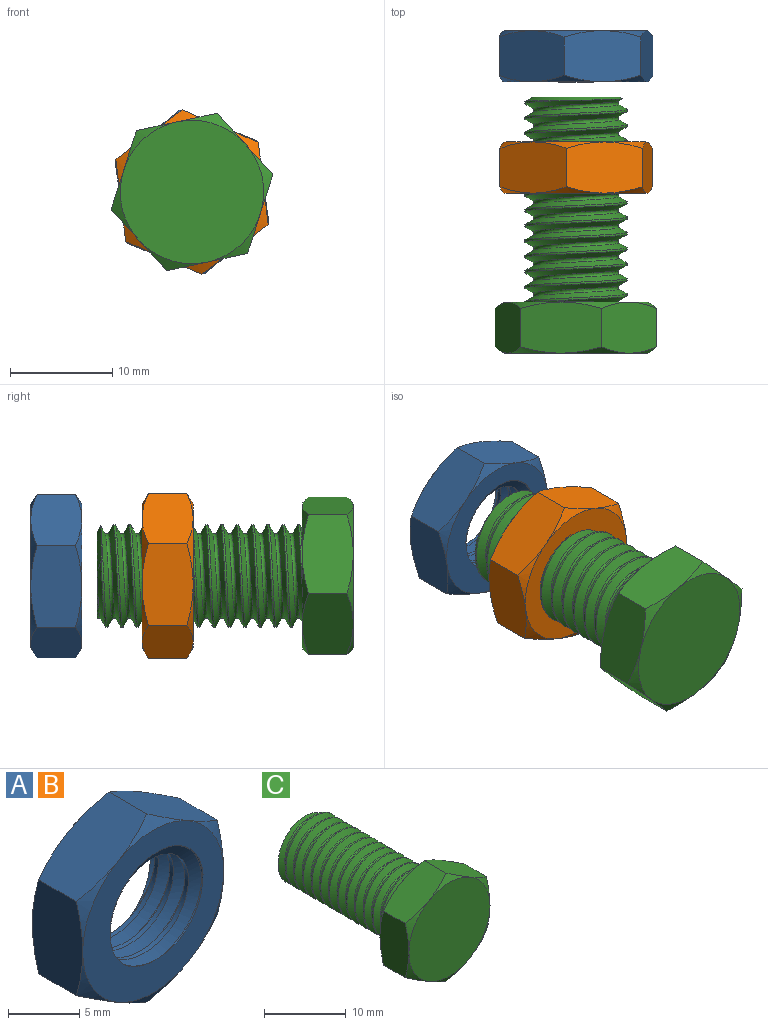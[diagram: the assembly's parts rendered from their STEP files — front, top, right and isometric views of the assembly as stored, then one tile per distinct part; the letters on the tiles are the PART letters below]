
ASSEMBLY  parts=3 mates=2
PART A: 24 faces, bbox 16.8x7x16.8 mm
  f0: plane 14.44x14.44mm, normal (0,-1,0), area 86.9mm2, adj f8,f9,f10,f11,f18,f19,f20,f21
  f1: plane 14.44x14.44mm, normal (0,1,0), area 86.9mm2, adj f8,f9,f10,f11,f12,f13,f14,f15
  f2: plane 7.66x5.67mm, normal (0.5,0,-0.87), area 36.9mm2, adj f3,f7,f13,f17,f19,f23
  f3: plane 8.76x5.67mm, normal (1,0,0), area 36.9mm2, adj f2,f4,f16,f17,f22,f23
  f4: plane 7.66x5.67mm, normal (0.5,0,0.87), area 36.9mm2, adj f3,f5,f15,f16,f21,f22
  f5: plane 7.66x5.67mm, normal (-0.5,0,0.87), area 36.9mm2, adj f4,f6,f14,f15,f20,f21
  f6: plane 8.76x5.67mm, normal (-1,0,0), area 36.9mm2, adj f5,f7,f12,f14,f18,f20
  f7: plane 7.66x5.67mm, normal (-0.5,0,-0.87), area 36.9mm2, adj f2,f6,f12,f13,f18,f19
  f8: bspline ~11.69x10.12mm, area 91.2mm2, adj f0,f1,f10,f11
  f9: bspline ~11.69x10.12mm, area 91.5mm2, adj f0,f1,f10,f11
  f10: bspline ~11.85x10.26mm, area 23.2mm2, adj f0,f1,f8,f9
  f11: cylinder r=4.25mm len=8.5mm, axis (0,1,0), area 32.9mm2, adj f0,f1,f8,f9
  f12: cone r=7mm half-angle=60deg, axis (0,-1,0), area 4.8mm2, adj f1,f6,f7
  f13: cone r=7mm half-angle=60deg, axis (0,-1,0), area 4.8mm2, adj f1,f2,f7
  f14: cone r=7mm half-angle=60deg, axis (0,-1,0), area 4.8mm2, adj f1,f5,f6
  f15: cone r=7mm half-angle=60deg, axis (0,-1,0), area 4.8mm2, adj f1,f4,f5
  f16: cone r=7mm half-angle=60deg, axis (0,-1,0), area 4.8mm2, adj f1,f3,f4
  f17: cone r=7mm half-angle=60deg, axis (0,-1,0), area 4.8mm2, adj f1,f2,f3
  f18: cone r=7mm half-angle=60deg, axis (0,1,0), area 4.8mm2, adj f0,f6,f7
  f19: cone r=7mm half-angle=60deg, axis (0,1,0), area 4.8mm2, adj f0,f2,f7
  f20: cone r=7mm half-angle=60deg, axis (0,1,0), area 4.8mm2, adj f0,f5,f6
  f21: cone r=7mm half-angle=60deg, axis (0,1,0), area 4.8mm2, adj f0,f4,f5
  f22: cone r=7mm half-angle=60deg, axis (0,1,0), area 4.8mm2, adj f0,f3,f4
  f23: cone r=7mm half-angle=60deg, axis (0,1,0), area 4.8mm2, adj f0,f2,f3
PART B: same geometry as A
PART C: 26 faces, bbox 16.8x26.3x16.8 mm
  f0: plane 14.42x14.42mm, normal (0,1,0), area 89.2mm2, adj f2,f3,f4,f5,f7,f8,f9,f10
  f1: plane 8.56x8.47mm, normal (0,1,0), area 55.9mm2, adj f3,f4,f5,f6
  f2: cylinder r=5mm len=19.63mm, axis (0,-1,0), area 140.7mm2, adj f0,f4,f5,f6
  f3: bspline ~21.13x9.67mm, area 146.9mm2, adj f0,f1,f4,f5
  f4: bspline ~21.22x11.55mm, area 355.2mm2, adj f0,f1,f2,f3,f6
  f5: bspline ~20.72x11.55mm, area 355.3mm2, adj f0,f1,f2,f3,f6
  f6: cone r=5mm half-angle=63.4deg, axis (0,-1,0), area 9.9mm2, adj f1,f2,f4,f5
  f7: cone r=7mm half-angle=60deg, axis (0,-1,0), area 4.8mm2, adj f0,f13,f18
  f8: cone r=7mm half-angle=60deg, axis (0,-1,0), area 4.8mm2, adj f0,f13,f14
  f9: cone r=7mm half-angle=60deg, axis (0,-1,0), area 4.8mm2, adj f0,f14,f15
  f10: cone r=7mm half-angle=60deg, axis (0,-1,0), area 4.8mm2, adj f0,f15,f16
  f11: cone r=7mm half-angle=60deg, axis (0,-1,0), area 4.8mm2, adj f0,f16,f17
  f12: cone r=7mm half-angle=60deg, axis (0,-1,0), area 4.8mm2, adj f0,f17,f18
  f13: plane 7.66x5.67mm, normal (-0.5,0,-0.87), area 36.9mm2, adj f7,f8,f14,f18,f20,f24
  f14: plane 8.76x5.67mm, normal (-1,0,0), area 36.9mm2, adj f8,f9,f13,f15,f23,f24
  f15: plane 7.66x5.67mm, normal (-0.5,0,0.87), area 36.9mm2, adj f9,f10,f14,f16,f22,f23
  f16: plane 7.66x5.67mm, normal (0.5,0,0.87), area 36.9mm2, adj f10,f11,f15,f17,f21,f22
  f17: plane 8.76x5.67mm, normal (1,0,0), area 36.9mm2, adj f11,f12,f16,f18,f19,f21
  f18: plane 7.66x5.67mm, normal (0.5,0,-0.87), area 36.9mm2, adj f7,f12,f13,f17,f19,f20
  f19: cone r=7mm half-angle=60deg, axis (0,1,0), area 4.8mm2, adj f17,f18,f25
  f20: cone r=7mm half-angle=60deg, axis (0,1,0), area 4.8mm2, adj f13,f18,f25
  f21: cone r=7mm half-angle=60deg, axis (0,1,0), area 4.8mm2, adj f16,f17,f25
  f22: cone r=7mm half-angle=60deg, axis (0,1,0), area 4.8mm2, adj f15,f16,f25
  f23: cone r=7mm half-angle=60deg, axis (0,1,0), area 4.8mm2, adj f14,f15,f25
  f24: cone r=7mm half-angle=60deg, axis (0,1,0), area 4.8mm2, adj f13,f14,f25
  f25: plane 14x14mm, normal (0,-1,0), area 153.9mm2, adj f19,f20,f21,f22,f23,f24
PLACE A rot(axis=(0,-1,0),8.3deg) t=(-8.24,28.32,4.17)mm
PLACE B rot(axis=(0.83,0,0.55),180deg) t=(-8.24,22.45,4.17)mm
PLACE C rot(axis=(0,1,0),77.8deg) t=(-8.24,6.82,4.17)mm fixed
MATE cylindrical B.f11 <-> C.f7  axis (0,1,0) through (-8.24,22.45,4.17)mm
MATE cylindrical C.f7 <-> A.f11  axis (0,-1,0) through (-8.24,1.67,4.17)mm
